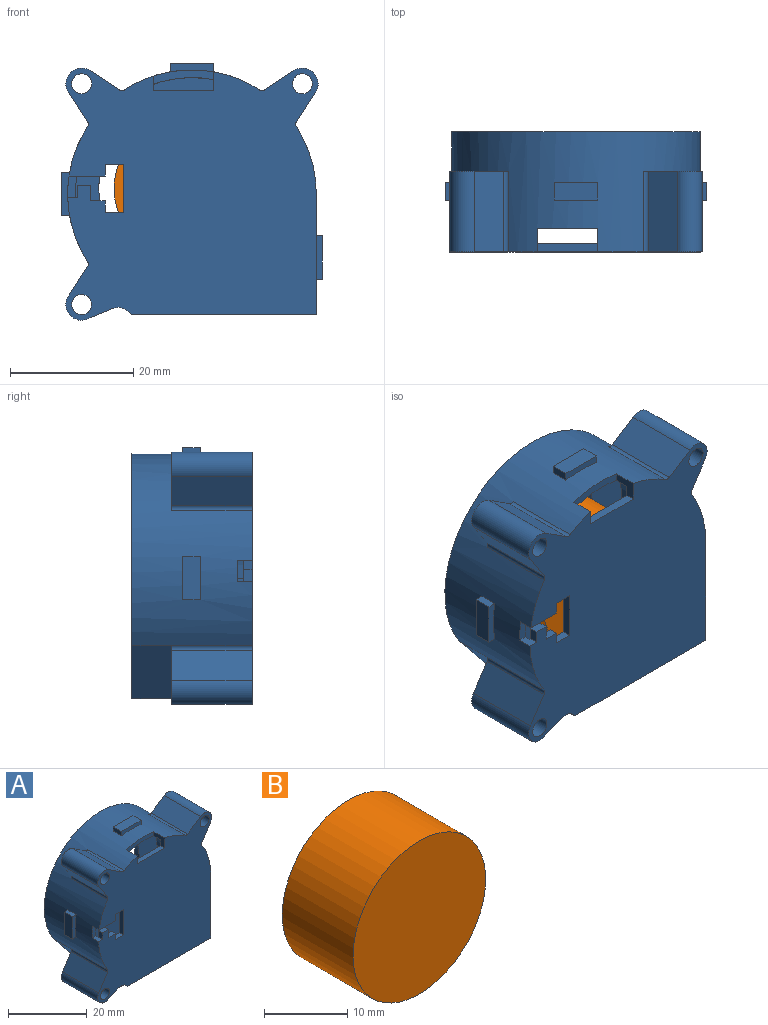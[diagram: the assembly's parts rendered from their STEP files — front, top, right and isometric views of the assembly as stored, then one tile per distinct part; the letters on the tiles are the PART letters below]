
ASSEMBLY  parts=2 mates=1
PART A: 65 faces, bbox 42.3x19.5x41.6 mm
  f0: cylinder r=18.89mm len=37.78mm, axis (0,1,0), area 1341.9mm2, adj f2,f3,f4,f32,f50,f51,f52,f62
  f1: plane 40.87x40.87mm, normal (0,-1,0), area 1391.6mm2, adj f7,f8,f9,f10,f11,f12,f13,f14
  f2: plane 38.11x37.77mm, normal (0,1,0), area 1162.8mm2, adj f0,f3,f4,f15,f49,f50,f51,f53
  f3: plane 16.55x2.09mm, normal (0.63,0,-0.77), area 44.6mm2, adj f0,f2,f15,f32
  f4: plane 19.56x16.55mm, normal (-1,0,0), area 323.6mm2, adj f0,f2,f15,f32
  f5: plane 9.51x9.51mm, normal (0,1,0), area 35.2mm2, adj f8,f17,f18,f19,f20,f21,f28
  f6: plane 9.51x9.51mm, normal (0,1,0), area 35.2mm2, adj f7,f8,f22,f23,f24,f26,f27
  f7: cylinder r=0.76mm len=13.05mm, axis (0,1,0), area 11.5mm2, adj f1,f6,f8,f26
  f8: cylinder r=20.14mm len=40.28mm, axis (0,1,0), area 1148.8mm2, adj f1,f5,f6,f7,f9,f16,f17,f21
  f9: cylinder r=0.76mm len=13.05mm, axis (0,1,0), area 11.5mm2, adj f1,f8,f10,f29
  f10: plane 13.05x4.74mm, normal (-0.84,0,0.55), area 73.9mm2, adj f1,f9,f11,f29
  f11: cylinder r=2.54mm len=13.05mm, axis (0,1,0), area 90.6mm2, adj f1,f10,f12,f29
  f12: plane 13.05x3.59mm, normal (0.38,0,-0.92), area 50.7mm2, adj f1,f11,f13,f29
  f13: cylinder r=2.4mm len=13.05mm, axis (0,1,0), area 39.7mm2, adj f1,f12,f14,f29
  f14: plane 13.06x0.36mm, normal (-0.77,0,-0.64), area 5.9mm2, adj f1,f13,f15,f31
  f15: plane 30x19.5mm, normal (0,0,-1), area 135.5mm2, adj f1,f2,f3,f4,f14,f16,f30,f31
  f16: plane 19.56x19.5mm, normal (1,0,0), area 361mm2, adj f1,f8,f15,f30,f44,f45,f47,f48
  f17: cylinder r=0.76mm len=13.05mm, axis (0,1,0), area 11.5mm2, adj f1,f5,f8,f18
  f18: plane 13.05x4.74mm, normal (0.84,0,-0.55), area 73.9mm2, adj f1,f5,f17,f19
  f19: cylinder r=2.54mm len=13.05mm, axis (0,1,0), area 90.6mm2, adj f1,f5,f18,f20
  f20: plane 13.05x4.74mm, normal (-0.55,0,0.84), area 73.9mm2, adj f1,f5,f19,f21
  f21: cylinder r=0.76mm len=13.05mm, axis (0,1,0), area 11.5mm2, adj f1,f5,f8,f20
  f22: cylinder r=0.76mm len=13.05mm, axis (0,1,0), area 11.5mm2, adj f1,f6,f8,f23
  f23: plane 13.05x4.74mm, normal (0.55,0,0.84), area 73.9mm2, adj f1,f6,f22,f24
  f24: cylinder r=2.54mm len=13.05mm, axis (0,1,0), area 90.6mm2, adj f1,f6,f23,f26
  f25: cylinder r=1.62mm len=13.05mm, axis (0,1,0), area 133.2mm2, adj f1,f29
  f26: plane 13.05x4.74mm, normal (-0.84,0,-0.55), area 73.9mm2, adj f1,f6,f7,f24
  f27: cylinder r=1.62mm len=13.05mm, axis (0,1,0), area 133.2mm2, adj f1,f6
  f28: cylinder r=1.62mm len=13.05mm, axis (0,1,0), area 133.2mm2, adj f1,f5
  f29: plane 10.29x9.51mm, normal (0,1,0), area 38mm2, adj f9,f10,f11,f12,f13,f25,f31
  f30: plane 40.28x39.7mm, normal (0,1,0), area 761.3mm2, adj f8,f15,f16,f31,f33
  f31: plane 8.64x7.07mm, normal (-0.77,0,-0.63), area 71.9mm2, adj f8,f14,f15,f29,f30
  f32: plane 38.45x37.78mm, normal (0,-1,0), area 624.2mm2, adj f0,f3,f4,f15,f33
  f33: cylinder r=13.75mm len=27.5mm, axis (0,-1,0), area 129.6mm2, adj f30,f32
  f34: plane 2.9x1.31mm, normal (1,0,0), area 3.8mm2, adj f8,f35,f37,f38
  f35: plane 7x2.9mm, normal (0,0,1), area 20.3mm2, adj f34,f36,f37,f38
  f36: plane 2.9x1.31mm, normal (-1,0,0), area 3.8mm2, adj f8,f35,f37,f38
  f37: plane 7x1.31mm, normal (0,-1,0), area 7.7mm2, adj f8,f34,f35,f36
  f38: plane 7x1.31mm, normal (0,1,0), area 7.7mm2, adj f8,f34,f35,f36
  f39: plane 7x2.9mm, normal (-1,0,0), area 20.3mm2, adj f40,f41,f42,f43
  f40: plane 2.9x1.31mm, normal (0,0,-1), area 3.8mm2, adj f8,f39,f42,f43
  f41: plane 2.9x1.31mm, normal (0,0,1), area 3.8mm2, adj f8,f39,f42,f43
  f42: plane 7x1.31mm, normal (0,-1,0), area 7.7mm2, adj f8,f39,f40,f41
  f43: plane 7x1.31mm, normal (0,1,0), area 7.7mm2, adj f8,f39,f40,f41
  f44: plane 2.9x1mm, normal (0,0,1), area 2.9mm2, adj f16,f46,f47,f48
  f45: plane 2.9x1mm, normal (0,0,-1), area 2.9mm2, adj f16,f46,f47,f48
  f46: plane 7x2.9mm, normal (1,0,0), area 20.3mm2, adj f44,f45,f47,f48
  f47: plane 7x1mm, normal (0,-1,0), area 7mm2, adj f16,f44,f45,f46
  f48: plane 7x1mm, normal (0,1,0), area 7mm2, adj f16,f44,f45,f46
  f49: plane 9.8x1.45mm, normal (0,0,1), area 14.2mm2, adj f1,f2,f50,f51
  f50: plane 3.85x3.08mm, normal (-1,0,0), area 7.5mm2, adj f0,f1,f2,f8,f49,f52
  f51: plane 3.85x2.4mm, normal (1,0,0), area 6.6mm2, adj f0,f1,f2,f8,f49,f52
  f52: plane 9.8x2.32mm, normal (0,-1,0), area 12.4mm2, adj f0,f8,f50,f51
  f53: plane 2x1.45mm, normal (-1,0,0), area 2.9mm2, adj f1,f2,f54,f62
  f54: plane 2.2x1.45mm, normal (0,0,1), area 3.2mm2, adj f1,f2,f53,f55
  f55: plane 2.5x1.45mm, normal (1,0,0), area 3.6mm2, adj f1,f2,f54,f56
  f56: plane 2.35x1.45mm, normal (0,0,1), area 3.4mm2, adj f1,f2,f55,f57
  f57: plane 1.92x1.45mm, normal (1,0,0), area 2.8mm2, adj f1,f2,f56,f58
  f58: plane 3x1.45mm, normal (0,0,1), area 4.4mm2, adj f1,f2,f57,f59
  f59: plane 7.84x1.45mm, normal (-1,0,0), area 11.4mm2, adj f1,f2,f58,f60
  f60: plane 3x1.45mm, normal (0,0,-1), area 4.4mm2, adj f1,f2,f59,f61
  f61: plane 1.92x1.45mm, normal (1,0,0), area 2.8mm2, adj f1,f2,f60,f63
  f62: plane 2.35x1.51mm, normal (0,0,1), area 3.3mm2, adj f0,f1,f2,f8,f53,f64
  f63: plane 5.85x2.35mm, normal (0,0,-1), area 9.6mm2, adj f0,f1,f2,f8,f61,f64
  f64: plane 3.5x1.48mm, normal (0,-1,0), area 4.4mm2, adj f0,f8,f62,f63
PART B: 3 faces, bbox 22.5x12x22.5 mm
  f0: cylinder r=11.25mm len=22.5mm, axis (0,-1,0), area 848.2mm2, adj f1,f2
  f1: plane 22.5x22.5mm, normal (0,1,0), area 397.6mm2, adj f0
  f2: plane 22.5x22.5mm, normal (0,-1,0), area 397.6mm2, adj f0
PLACE A t=(-31.02,30.22,8.51)mm
PLACE B t=(-31.02,32.27,8.51)mm
MATE fastened A.f33 <-> B.f0  axis (0,1,0) through (-32.38,39.87,9.45)mm
